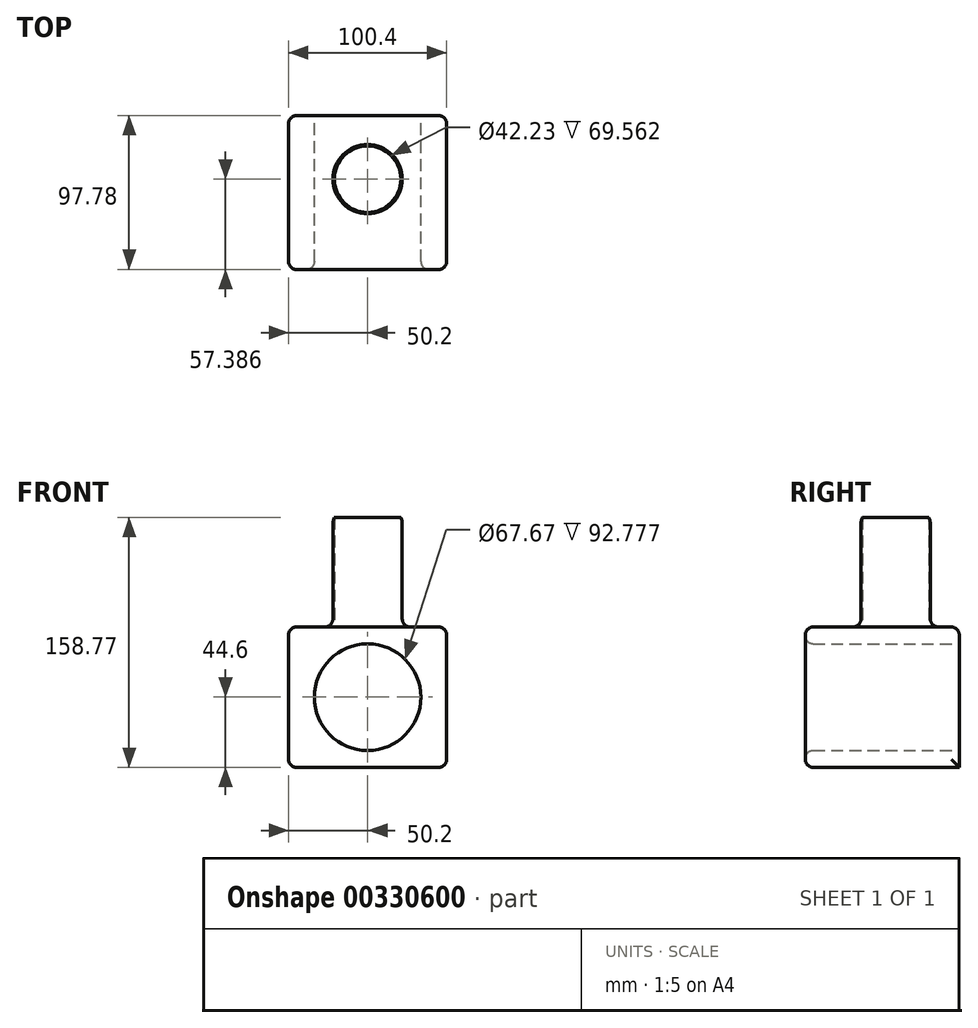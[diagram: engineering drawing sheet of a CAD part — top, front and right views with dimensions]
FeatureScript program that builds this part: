
annotation { "Feature Type Name" : "Feature", "Feature Type Description" : "" }
export const myFeature = defineFeature(function(context is Context, id is Id, definition is map)
    precondition{}
    {
        {
            var Q0;
            Q0=qCreatedBy(makeId("Front.planeOp"),FACE);
            var sketch = newSketch(context, id + "F0", { "sketchPlane" : qUnion([Q0])});
            skLineSegment(sketch, "E0.bottom", {"start": v(50.2, -44.6) * mm, "end": v(-50.2, -44.6) * mm});
            skLineSegment(sketch, "E0.top", {"start": v(50.2, 44.6) * mm, "end": v(-50.2, 44.6) * mm});
            skLineSegment(sketch, "E0.left", {"start": v(50.2, -44.6) * mm, "end": v(50.2, 44.6) * mm});
            skLineSegment(sketch, "E0.right", {"start": v(-50.2, -44.6) * mm, "end": v(-50.2, 44.6) * mm});
            skPoint(sketch, "E0.middle", {"position": v(0, 0) * mm});
            skSolve(sketch);
        }
        {
            var Q0;
            Q0 = qSketchRegion(id + "F0", true);
            var Q1;
            Q1 = qBodyType(qCreatedBy(id + "F0" ,EDGE), BodyType.WIRE);
            extrude(context, id + "F1", {"entities" : qUnion([Q0]), "surfaceEntities" : qUnion([Q1]), "depth" : 97.78 * mm});
        }
        {
            var Q0;
            Q0=qCreatedBy(makeId("Top.planeOp"),FACE);
            var sketch = newSketch(context, id + "F2", { "sketchPlane" : qUnion([Q0])});
            skCircle(sketch, "E1", {"center": v(0, -40.4) * mm, "radius": 22.02 * mm});
            skCircle(sketch, "E2", {"center": v(0, -40.4) * mm, "radius": 21.12 * mm});
            skSolve(sketch);
        }
        {
            var Q0;
            Q0 = qSketchRegion(id + "F2", true);
            extrude(context, id + "F3", {"entities" : qUnion([Q0]), "operationType" : NewBodyOperationType.ADD, "depth" : 114.17 * mm});
        }
        {
            var Q0;
            {var subQ1=sQuery(id+"F0.wireOp",EDGE,"E0.left");var subQ2=sQuery(id+"F0.wireOp",EDGE,"E0.top");Q0=makeQuery(id+"F3.boolean.opBoolean","SPLIT",FACE,{"disambiguationData":[TD([makeQuery(id+"F1.opExtrude","SWEPT_FACE",FACE,{"disambiguationData":[OSD([subQ1])]})])],"derivedFrom":makeQuery(id+"F1.opExtrude","SWEPT_FACE",FACE,{"disambiguationData":[OSD([subQ2])]})});}
            var Q1;
            Q1=makeQuery(id+"F1.opExtrude","CAP_FACE",FACE,{"disambiguationData":[OSD([sQuery(id+"F0.wireOp",EDGE,"E0.bottom"),sQuery(id+"F0.wireOp",EDGE,"E0.top"),sQuery(id+"F0.wireOp",EDGE,"E0.left"),sQuery(id+"F0.wireOp",EDGE,"E0.right")])],"isStart":false});
            var Q2;
            Q2=makeQuery(id+"F1.opExtrude","SWEPT_FACE",FACE,{"disambiguationData":[OSD([sQuery(id+"F0.wireOp",EDGE,"E0.right")])]});
            var Q3;
            Q3=makeQuery(id+"F1.opExtrude","SWEPT_FACE",FACE,{"disambiguationData":[OSD([sQuery(id+"F0.wireOp",EDGE,"E0.left")])]});
            fillet(context, id + "F4", {"entities" : qUnion([Q0, Q1, Q2, Q3]), "radius" : 5.08 * mm, "tangentPropagation" : true, "allowEdgeOverflow" : false});
        }
        {
            var Q0;
            Q0=qCreatedBy(makeId("Front.planeOp"),FACE);
            var sketch = newSketch(context, id + "F5", { "sketchPlane" : qUnion([Q0])});
            skCircle(sketch, "E3", {"center": v(0, 0) * mm, "radius": 33.84 * mm});
            skSolve(sketch);
        }
        {
            var Q0;
            Q0 = qSketchRegion(id + "F5", true);
            extrude(context, id + "F6", {"entities" : qUnion([Q0]), "operationType" : NewBodyOperationType.REMOVE, "depth" : 98.34 * mm});
        }
        {
            var Q0;
            Q0=makeQuery(id+"F1.opExtrude","SWEPT_FACE",FACE,{"disambiguationData":[OSD([sQuery(id+"F0.wireOp",EDGE,"E0.left")])]});
            var Q1;
            Q1=makeQuery(id+"F6.boolean.opBoolean","INTERSECT",EDGE,{"derivedFrom":[makeQuery(id+"F1.opExtrude","CAP_FACE",FACE,{"disambiguationData":[OSD([sQuery(id+"F0.wireOp",EDGE,"E0.bottom"),sQuery(id+"F0.wireOp",EDGE,"E0.top"),sQuery(id+"F0.wireOp",EDGE,"E0.left"),sQuery(id+"F0.wireOp",EDGE,"E0.right")])],"isStart":false}),makeQuery(id+"F6.opExtrude","SWEPT_FACE",FACE,{"disambiguationData":[OSD([sQuery(id+"F5.wireOp",EDGE,"E3")])]})]});
            fillet(context, id + "F7", {"entities" : qUnion([Q0, Q1]), "radius" : 5 * mm, "tangentPropagation" : true, "allowEdgeOverflow" : false});
        }
        {
            var Q0;
            Q0=qCreatedBy(makeId("Right.planeOp"),FACE);
            var sketch = newSketch(context, id + "F8", { "sketchPlane" : qUnion([Q0])});
            skCircle(sketch, "E4", {"center": v(39.94, 40.83) * mm, "radius": 16.83 * mm});
            skSolve(sketch);
        }
        {
            var Q0;
            Q0=sQuery(id+"F8.wireOp",EDGE,"E4");
            extrude(context, id + "F9", {"bodyType" : ToolBodyType.SURFACE, "surfaceEntities" : qUnion([Q0]), "oppositeDirection" : true, "depth" : 150 * mm});
        }
        {
            var Q0;
            Q0=makeQuery(id+"F3.opExtrude","CAP_EDGE",EDGE,{"disambiguationData":[OSD([sQuery(id+"F2.wireOp",EDGE,"E1")])],"isStart":false});
            fillet(context, id + "F10", {"entities" : qUnion([Q0]), "radius" : 10 * mm, "tangentPropagation" : true, "allowEdgeOverflow" : false});
        }
    });
